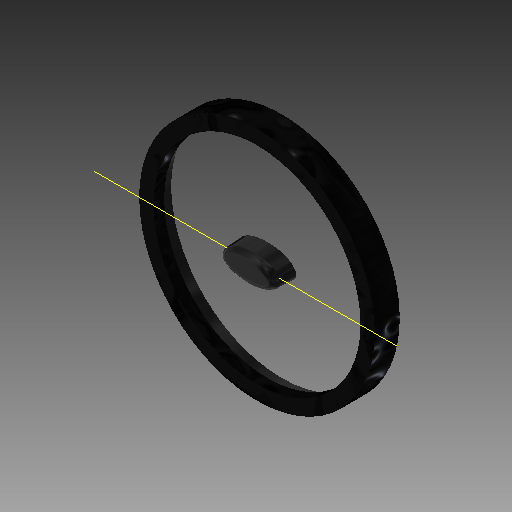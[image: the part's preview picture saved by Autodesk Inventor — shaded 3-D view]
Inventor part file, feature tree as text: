
AUTODESK INVENTOR PART (.ipt)
format: ipt  version: 2017.2 (Build 212233000, 233)  size: 675,840 bytes
history: native  units: in
note: dims shown in document units (in); Inventor stores cm internally (conversion verified against a paired STEP export)
features: sketch x23, extrude x17, plane x9, projected_geometry x5, loft x4, other x4, mirror x1, emboss x1, fillet x1
ambient origin geometry x8: Origin, YZ Plane, XZ Plane, XY Plane, X Axis, Y Axis, Z Axis, Center Point
bodies: Solid1 (feature_tree)
feature tree (65):
  sketch  "Sketch1"  dims[d0=0.7559in d1=0.7559in]
  plane  "Work Plane1"
  loft  "Loft1"
  extrude  "Extrusion1"  Depth=0.2in
  plane  "Work Plane4"
  loft  "Loft2"
  plane  "Work Plane5"
  loft  "Loft3"
  loft  "Loft4"
  extrude  "Extrusion2"  TaperAngle=0.0deg  [1 undecoded]
  plane  "Work Plane6"
  extrude  "Extrusion3"  Depth=1.0in
  extrude  "Extrusion4"  Depth=1.0651in
  extrude  "Extrusion5"  Depth=0.962in
  plane  "Work Plane7"
  extrude  "Extrusion6"  Depth=0.075in
  plane  "Work Plane8"
  other  "Work Axis1"
  plane  "Work Plane9"
  extrude  "Extrusion7"  Depth=0.06in
  mirror  "Mirror3"
  extrude  "Extrusion8"  Depth=0.05in
  plane  "Work Plane10"
  extrude  "Extrusion9"  Depth=0.0625in
  plane  "Work Plane11"
  extrude  "Extrusion10"  Depth=0.075in
  extrude  "Extrusion11"  TaperAngle=0.0deg  [1 undecoded]
  extrude  "Extrusion12"  Depth=0.2in
  extrude  "Extrusion13"  TaperAngle=0.0deg  [1 undecoded]
  emboss  "Emboss1"
  extrude  "Extrusion16"  Depth=0.01in
  extrude  "Extrusion17"  Depth=0.0344in
  extrude  "Extrusion18"  TaperAngle=60.0deg  [1 undecoded]
  fillet  "Fillet1"  [1 undecoded]
  extrude  "Extrusion20"  Depth=0.05in
  other  "Work Axis3"
  sketch  "Sketch2"  dims[d2=0.9963in d3=0.2in]
  sketch  "Sketch3"  dims[d4=0.5in d6=0.08in]
  sketch  "Sketch4"  dims[d7=0.55in d8=150.0deg]
  other  "Edges1"
  sketch  "Sketch5"  dims[d9=150.0deg d14=0.33in]
  projected_geometry  "Projected Loop1"
  other  "Edges2"
  sketch  "Sketch6"  dims[d15=0.66in d18=0.0in d19=90.0deg]
  sketch  "Sketch7"  dims[d20=0.0in d21=90.0deg d22=1.0in]
  sketch  "Sketch8"  dims[d26=1.0651in d28=1.0651in]
  sketch  "Sketch9"  dims[d29=0.0in d30=0.962in]
  sketch  "Sketch10"  dims[d31=0.962in d32=0.075in]
  sketch  "Sketch11"  dims[d33=0.15in d34=0.06in]
  sketch  "Sketch12"  dims[d35=0.1in d36=0.05in]
  sketch  "Sketch13"  dims[d37=0.45in d38=0.0in d39=0.0625in]
  projected_geometry  "Projected Loop2"
  projected_geometry  "Projected Loop3"
  sketch  "Sketch14"  dims[d40=0.01in d41=0.075in]
  projected_geometry  "Projected Loop4"
  sketch  "Sketch15"  dims[d42=0.01in d43=0.0in d44=90.0deg]
  sketch  "Sketch16"  dims[d45=0.0in d46=90.0deg d47=0.2in]
  sketch  "Sketch17"  dims[d48=0.07in d49=0.0in d50=90.0deg]
  sketch  "Sketch18"  dims[d51=0.0in d52=90.0deg d53=0.01in]
  sketch  "Sketch19"  dims[d54=0.01in d55=0.0344in]
  sketch  "Sketch23"  dims[d56=150.0deg d57=60.0deg d58=150.0deg]
  projected_geometry  "Projected Loop6"
  sketch  "Sketch24"  dims[d59=0.7in d60=0.05in]
  sketch  "Sketch25"  dims[d61=0.05in d62=0.05in]
  sketch  "Sketch27"  dims[d63=0.05in d64=0.05in d65=0.01in d66=0.0in d67=90.0deg d68=0.0in d69=90.0deg d70=0.1in d71=0.4in d72=0.15in d73=0.05in d74=0.0in d75=0.02in d77=0.15in d78=0.02in d79=0.1in d80=0.1in d81=0.1in d82=0.02in d83=0.15in d84=0.05in d85=0.0in d86=0.045in d87=0.0in d88=0.025in d89=0.0in d90=0.02in d91=0.02in d92=0.005in d93=0.0in d94=90.0deg d95=0.4466in d96=1.0in d97=0.0in d98=1.0in d99=0.0in d100=0.6528in d101=0.0in d102=0.0in d103=1.0in d104=0.0in d106=90.0deg d107=1.0in d108=0.0in d109=1.65in d110=0.1in d111=0.1in d112=0.0in d113=0.1in d114=0.075in d115=0.0in d116=0.05in d117=0.0in d123=0.84in d124=0.8in d125=0.0in d126=0.0in d127=1.0in d128=0.0in d130=0.15in d131=-0.0206in d135=0.2in d136=0.05in d137=0.1in d140=0.05in d141=0.1in d142=0.0in]
note: 5 required parameter values undecoded (feature->parameter linkage not recoverable at this tier; creation-order binding heuristic only, values carry confidence <= 0.55)
